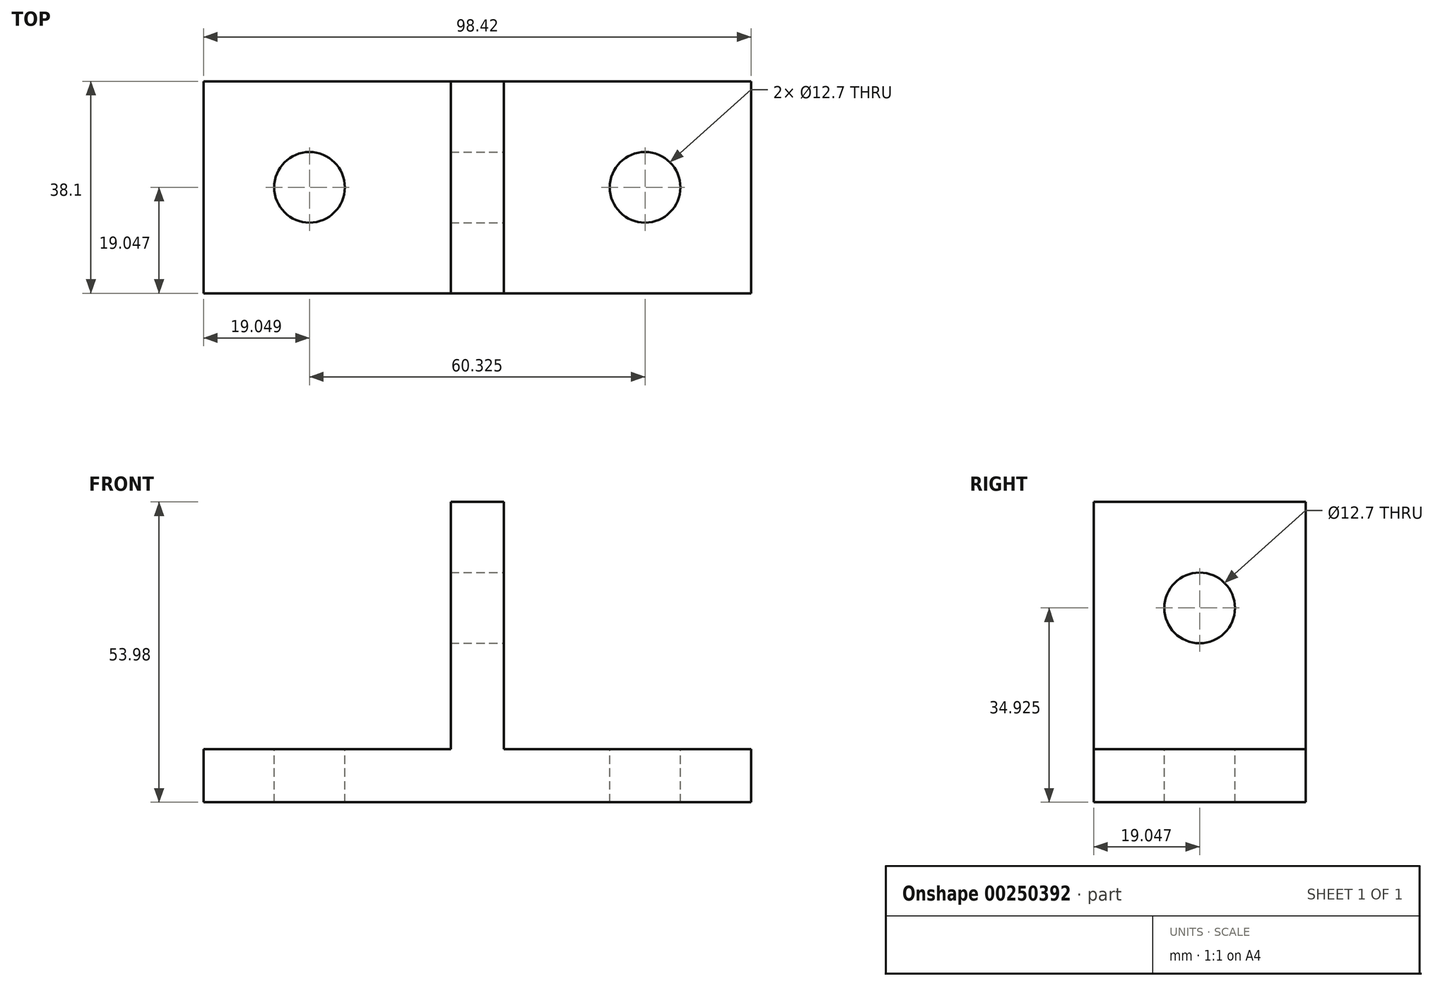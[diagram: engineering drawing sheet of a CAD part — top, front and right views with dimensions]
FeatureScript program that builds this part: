
annotation { "Feature Type Name" : "Feature", "Feature Type Description" : "" }
export const myFeature = defineFeature(function(context is Context, id is Id, definition is map)
    precondition{}
    {
        {
            var Q0;
            Q0=qCreatedBy(makeId("Top.planeOp"),FACE);
            var sketch = newSketch(context, id + "F0", { "sketchPlane" : qUnion([Q0])});
            skLineSegment(sketch, "E0", {"start": v(-76.45, 55.9) * mm, "end": v(-76.45, 17.8) * mm});
            skLineSegment(sketch, "E1", {"start": v(-76.45, 17.8) * mm, "end": v(21.97, 17.8) * mm});
            skLineSegment(sketch, "E2", {"start": v(21.97, 17.8) * mm, "end": v(21.97, 55.9) * mm});
            skLineSegment(sketch, "E3", {"start": v(21.97, 55.9) * mm, "end": v(-76.45, 55.9) * mm});
            skSolve(sketch);
        }
        {
            var Q0;
            Q0=makeQuery(id+"F0.imprint","IMPRINT",FACE,{"disambiguationData":[TD([[makeQuery(id+"F0.imprint","IMPRINT",EDGE,{"derivedFrom":sQuery(id+"F0.wireOp",EDGE,"E0")}),1.0]])]});
            extrude(context, id + "F1", {"entities" : qUnion([Q0]), "depth" : 9.52 * mm});
        }
        {
            var Q0;
            Q0=makeQuery(id+"F1.opExtrude","CAP_FACE",FACE,{"disambiguationData":[OSD([sQuery(id+"F0.wireOp",EDGE,"E0"),sQuery(id+"F0.wireOp",EDGE,"E1"),sQuery(id+"F0.wireOp",EDGE,"E2"),sQuery(id+"F0.wireOp",EDGE,"E3")])],"isStart":false});
            var sketch = newSketch(context, id + "F2", { "sketchPlane" : qUnion([Q0])});
            skLineSegment(sketch, "E4", {"start": v(21.97, 36.85) * mm, "end": v(2.92, 36.85) * mm});
            skLineSegment(sketch, "E5", {"start": v(-76.45, 36.85) * mm, "end": v(-57.4, 36.85) * mm});
            skSolve(sketch);
        }
        {
            var Q0;
            Q0=sQuery(id+"F2.wireOp",VERTEX,"E5.end");
            var Q1;
            Q1=sQuery(id+"F2.wireOp",VERTEX,"E4.end");
            var Q2;
            Q2=makeQuery(id+"F1.opExtrude","SWEPT_BODY",BODY,{"disambiguationData":[OSD([sQuery(id+"F0.wireOp",EDGE,"E0"),sQuery(id+"F0.wireOp",EDGE,"E1"),sQuery(id+"F0.wireOp",EDGE,"E2"),sQuery(id+"F0.wireOp",EDGE,"E3")])]});
            hole(context, id + "F3", {"style" : HoleStyle.SIMPLE, "endStyle" : HoleEndStyle.THROUGH, "holeDiameter" : 12.7 * mm, "tappedDepth" : 12.7 * mm, "tapClearance" : 3, "locations" : qUnion([Q0, Q1]), "scope" : qUnion([Q2])});
        }
        {
            var Q0;
            Q0=makeQuery(id+"F1.opExtrude","CAP_FACE",FACE,{"disambiguationData":[OSD([sQuery(id+"F0.wireOp",EDGE,"E0"),sQuery(id+"F0.wireOp",EDGE,"E1"),sQuery(id+"F0.wireOp",EDGE,"E2"),sQuery(id+"F0.wireOp",EDGE,"E3")])],"isStart":false});
            var sketch = newSketch(context, id + "F4", { "sketchPlane" : qUnion([Q0])});
            skLineSegment(sketch, "E6.bottom", {"start": v(-27.24, 17.8) * mm, "end": v(-32, 17.8) * mm});
            skLineSegment(sketch, "E6.top", {"start": v(-27.24, 55.9) * mm, "end": v(-32, 55.9) * mm});
            skLineSegment(sketch, "E6.right", {"start": v(-32, 17.8) * mm, "end": v(-32, 55.9) * mm});
            skLineSegment(sketch, "E7.bottom", {"start": v(-27.24, 17.8) * mm, "end": v(-22.48, 17.8) * mm});
            skLineSegment(sketch, "E7.top", {"start": v(-27.24, 55.9) * mm, "end": v(-22.48, 55.9) * mm});
            skLineSegment(sketch, "E7.right", {"start": v(-22.48, 17.8) * mm, "end": v(-22.48, 55.9) * mm});
            skSolve(sketch);
        }
        {
            var Q0;
            Q0=makeQuery(id+"F4.imprint","IMPRINT",FACE,{"disambiguationData":[TD([[makeQuery(id+"F4.imprint","IMPRINT",EDGE,{"derivedFrom":sQuery(id+"F4.wireOp",EDGE,"E6.bottom")}),1.0]])]});
            extrude(context, id + "F5", {"entities" : qUnion([Q0]), "operationType" : NewBodyOperationType.ADD, "depth" : 44.45 * mm});
        }
        {
            var Q0;
            Q0=makeQuery(id+"F5.opExtrude","SWEPT_FACE",FACE,{"disambiguationData":[OSD([sQuery(id+"F4.wireOp",EDGE,"E7.right")])]});
            var sketch = newSketch(context, id + "F6", { "sketchPlane" : qUnion([Q0])});
            skLineSegment(sketch, "E8", {"start": v(36.85, 53.98) * mm, "end": v(36.85, 34.92) * mm});
            skSolve(sketch);
        }
        {
            var Q0;
            Q0=sQuery(id+"F6.wireOp",VERTEX,"E8.end");
            var Q1;
            Q1=makeQuery(id+"F1.opExtrude","SWEPT_BODY",BODY,{"disambiguationData":[OSD([sQuery(id+"F0.wireOp",EDGE,"E0"),sQuery(id+"F0.wireOp",EDGE,"E1"),sQuery(id+"F0.wireOp",EDGE,"E2"),sQuery(id+"F0.wireOp",EDGE,"E3")])]});
            hole(context, id + "F7", {"style" : HoleStyle.SIMPLE, "endStyle" : HoleEndStyle.THROUGH, "holeDiameter" : 12.7 * mm, "tappedDepth" : 12.7 * mm, "tapClearance" : 3, "locations" : qUnion([Q0]), "scope" : qUnion([Q1])});
        }
    });
